# Revit family: Plumbing_Valves_Bermad_420_Pressure_Reducing_Valve Grooved 2in-8in
name_source: partatom
category: Pipe Accessories
units: mm (PartAtom-declared; Revit-internal decimal feet)

## family parameters
Always vertical = No
Cut with Voids When Loaded = No
Part Type = Valve - Breaks Into
Round Connector Dimension = Use Diameter
Shared = No
Work Plane-Based = No

## types (5) — shared parameters
Assembly Code = D2020300
Body_Type = Grooved
D_Table = 400 Revit Sizes
Description = Pressure Reducing Valve
Flanged_Body = No
Grooved_Body = Yes
M = 160 mm
Manufacturer = Bermad
Max Working Water Pressure = 16.0 bar
Max Working Water Temperature = 50 °C
Model = 420
Product url = www.bermad.com/product/bc-420-p/
T_from_port = 220 mm
Threaded_Body = No
URL = www.Bermad.com

## per-type parameters (varying)
- 2" - DN50: Body_Dim=64 mm; CChamper_Rad=11 mm  [stored 0.0360892 ft]; CPort_Dim=40 mm  [stored 0.131234 ft]; Cover_Dim=118 mm; Flange_Dim=60 mm  [stored 0.19685 ft]; Flange_Thick=16 mm  [stored 0.0524934 ft]; H=115 mm; H1=29 mm  [stored 0.0951444 ft]; H2=11 mm  [stored 0.0360892 ft]; H2_Plus_H3=25 mm  [stored 0.082021 ft]; H3=14 mm  [stored 0.0459318 ft]; H4=17 mm  [stored 0.0557743 ft]; H5=4 mm  [stored 0.0131234 ft]; H5_Plus_H6=7 mm; H6=3 mm  [stored 0.00984252 ft]; H_Plus_M=275 mm; K Coefficient=57; L=205 mm; Nominal_Diameter=50 mm  [stored 0.164042 ft]; Port_Dim=30 mm  [stored 0.0984252 ft]; Port_Down_X=59 mm  [stored 0.19357 ft]; Port_Down_Y=11 mm  [stored 0.0360892 ft]; Port_Up_X=54 mm  [stored 0.177165 ft]; Port_Up_Y=5 mm  [stored 0.0164042 ft]; Port_W=50 mm  [stored 0.164042 ft]; Port_h=35 mm  [stored 0.114829 ft]; Port_h_Dim=42 mm  [stored 0.137795 ft]; Port_h_X=45 mm  [stored 0.147638 ft]; W=118 mm; Weight=5.00 kgf; h=35 mm  [stored 0.114829 ft]
- 3" - DN80: Body_Dim=93 mm; CChamper_Rad=11 mm  [stored 0.0360892 ft]; CPort_Dim=40 mm  [stored 0.131234 ft]; Cover_Dim=170 mm; Flange_Dim=89 mm; Flange_Thick=16 mm  [stored 0.0524934 ft]; H=165 mm; H1=40 mm  [stored 0.131234 ft]; H2=17 mm  [stored 0.0557743 ft]; H2_Plus_H3=35 mm  [stored 0.114829 ft]; H3=18 mm  [stored 0.0590551 ft]; H4=22 mm  [stored 0.0721785 ft]; H5=9 mm  [stored 0.0295276 ft]; H5_Plus_H6=11 mm  [stored 0.0360892 ft]; H6=2 mm  [stored 0.00656168 ft]; H_Plus_M=325 mm; K Coefficient=136; L=250 mm; Nominal_Diameter=80 mm; Port_Dim=30 mm  [stored 0.0984252 ft]; Port_Down_X=78 mm; Port_Down_Y=18 mm  [stored 0.0590551 ft]; Port_Up_X=75 mm; Port_Up_Y=13 mm  [stored 0.0426509 ft]; Port_W=68 mm; Port_h=57 mm  [stored 0.187008 ft]; Port_h_Dim=60 mm  [stored 0.19685 ft]; Port_h_X=53 mm  [stored 0.173885 ft]; W=170 mm; Weight=10.60 kgf; h=57 mm  [stored 0.187008 ft]
- 4" - DN100: Body_Dim=121 mm; CChamper_Rad=14 mm  [stored 0.0459318 ft]; CPort_Dim=40 mm  [stored 0.131234 ft]; Cover_Dim=205 mm; Flange_Dim=114 mm; Flange_Thick=16 mm  [stored 0.0524934 ft]; H=198 mm; H1=49 mm  [stored 0.160761 ft]; H2=27 mm  [stored 0.0885827 ft]; H2_Plus_H3=49 mm  [stored 0.160761 ft]; H3=22 mm  [stored 0.0721785 ft]; H4=27 mm  [stored 0.0885827 ft]; H5=6 mm  [stored 0.019685 ft]; H5_Plus_H6=9 mm  [stored 0.0295276 ft]; H6=3 mm  [stored 0.00984252 ft]; H_Plus_M=358 mm; K Coefficient=204; L=320 mm; Nominal_Diameter=100 mm; Port_Dim=35 mm  [stored 0.114829 ft]; Port_Down_X=107 mm; Port_Down_Y=22 mm  [stored 0.0721785 ft]; Port_Up_X=107 mm; Port_Up_Y=17 mm  [stored 0.0557743 ft]; Port_W=75 mm; Port_h=64 mm; Port_h_Dim=80 mm; Port_h_X=55 mm  [stored 0.180446 ft]; W=205 mm; Weight=16.20 kgf; h=64 mm
- 6" - DN150: Body_Dim=172 mm; CChamper_Rad=16 mm  [stored 0.0524934 ft]; CPort_Dim=80 mm; Cover_Dim=290 mm; Flange_Dim=168 mm; Flange_Thick=16 mm  [stored 0.0524934 ft]; H=301 mm; H1=71 mm; H2=33 mm  [stored 0.108268 ft]; H2_Plus_H3=73 mm; H3=40 mm  [stored 0.131234 ft]; H4=46 mm; H5=11 mm  [stored 0.0360892 ft]; H5_Plus_H6=12 mm  [stored 0.0393701 ft]; H6=1 mm  [stored 0.00328084 ft]; H_Plus_M=461 mm; K Coefficient=458; L=415 mm; Nominal_Diameter=150 mm; Port_Dim=40 mm  [stored 0.131234 ft]; Port_Down_X=122 mm; Port_Down_Y=40 mm  [stored 0.131234 ft]; Port_Up_X=122 mm; Port_Up_Y=25 mm  [stored 0.082021 ft]; Port_W=121 mm; Port_h=98 mm; Port_h_Dim=80 mm; Port_h_X=110 mm; W=290 mm; Weight=49.00 kgf; h=98 mm
- 8" - DN200: Body_Dim=224 mm; CChamper_Rad=56 mm  [stored 0.183727 ft]; CPort_Dim=80 mm; Cover_Dim=361 mm; Flange_Dim=219 mm; Flange_Thick=19 mm  [stored 0.062336 ft]; H=409 mm; H1=112 mm; H2=44 mm; H2_Plus_H3=94 mm; H3=49 mm  [stored 0.160761 ft]; H4=61 mm; H5=20 mm  [stored 0.0656168 ft]; H5_Plus_H6=21 mm; H6=1 mm  [stored 0.00328084 ft]; H_Plus_M=569 mm; K Coefficient=781; L=500 mm; Nominal_Diameter=200 mm; Port_Dim=40 mm  [stored 0.131234 ft]; Port_Down_X=150 mm; Port_Down_Y=45 mm  [stored 0.147638 ft]; Port_Up_X=150 mm; Port_Up_Y=33 mm  [stored 0.108268 ft]; Port_W=130 mm; Port_h=122 mm; Port_h_Dim=80 mm; Port_h_X=150 mm; W=361 mm; Weight=108.00 kgf; h=122 mm

note: [stored X ft] marks values corroborated as IEEE doubles in the binary element streams (Revit-internal decimal feet)

## geometry (parser evidence)
native form markers: Sweep x1
no freeform markers — native parametric forms only
